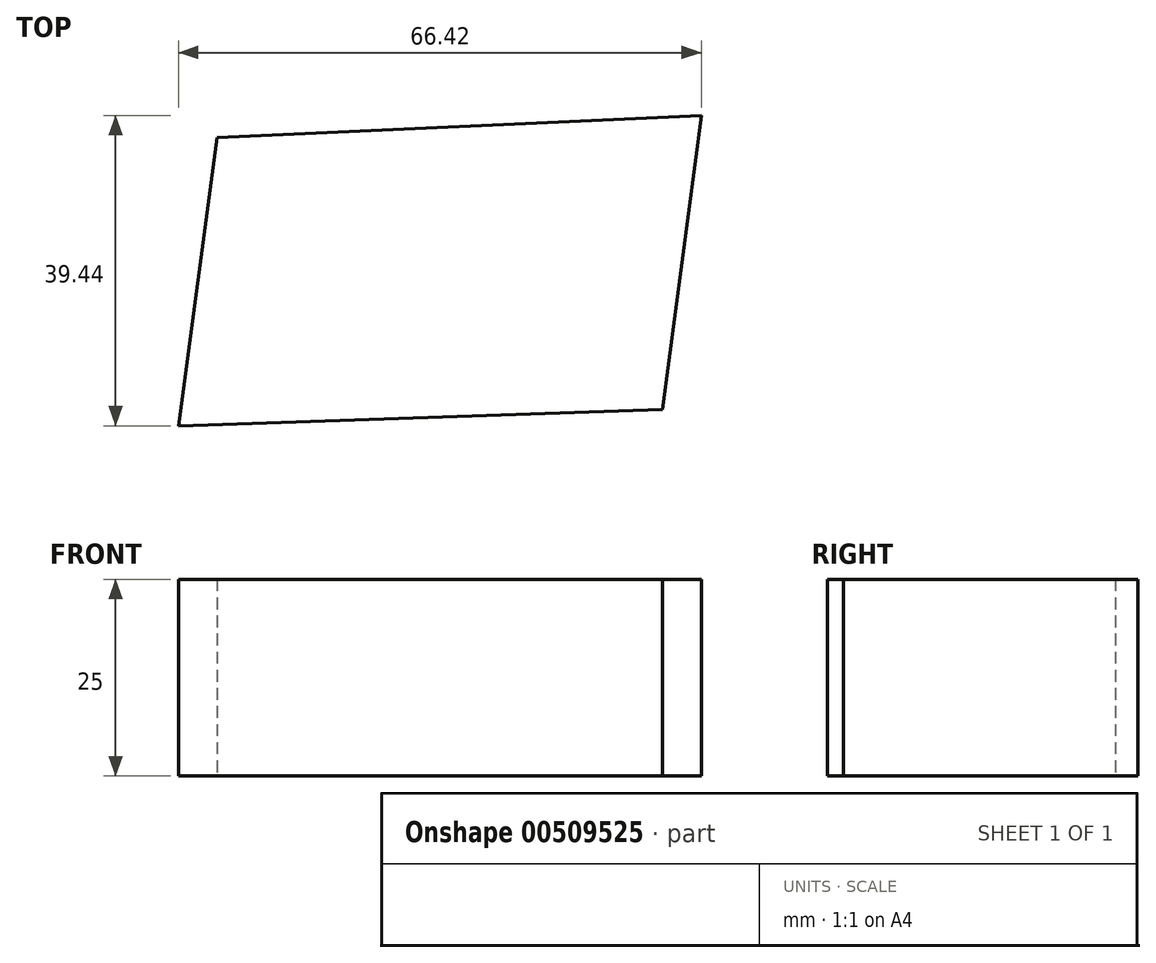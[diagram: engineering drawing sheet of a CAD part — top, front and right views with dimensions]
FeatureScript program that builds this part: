
annotation { "Feature Type Name" : "Feature", "Feature Type Description" : "" }
export const myFeature = defineFeature(function(context is Context, id is Id, definition is map)
    precondition{}
    {
        {
            var Q0;
            Q0=qCreatedBy(makeId("Top.planeOp"),FACE);
            var sketch = newSketch(context, id + "F0", { "sketchPlane" : qUnion([Q0])});
            skLineSegment(sketch, "E0", {"start": v(-44.45, -10.22) * mm, "end": v(18.23, -8.1) * mm});
            skLineSegment(sketch, "E1", {"start": v(18.23, -8.1) * mm, "end": v(23.15, 29.26) * mm});
            skLineSegment(sketch, "E2", {"start": v(23.15, 29.26) * mm, "end": v(-38.34, 26.43) * mm});
            skLineSegment(sketch, "E3", {"start": v(-38.34, 26.43) * mm, "end": v(-43.32, -10.58) * mm});
            skSolve(sketch);
        }
        {
            var Q0;
            Q0 = qSketchRegion(id + "F0", true);
            extrude(context, id + "F1", {"entities" : qUnion([Q0]), "depth" : 25 * mm});
        }
    });
